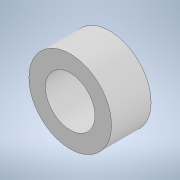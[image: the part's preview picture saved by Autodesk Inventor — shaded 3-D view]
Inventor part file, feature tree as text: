
AUTODESK INVENTOR PART (.ipt)
format: ipt  version: 2022 (Build 260153000, 153)  size: 98,816 bytes
history: native  units: mm
features: extrude x1, sketch x1
ambient origin geometry x8: Origin, YZ Plane, XZ Plane, XY Plane, X Axis, Y Axis, Z Axis, Center Point
bodies: Solid1 (feature_tree)
feature tree (2):
  extrude  "Extrusion1"  Depth=12.0mm
  sketch  "Sketch1"  dims[d0=15.0mm d1=25.0mm d2=12.0mm d3=0.0mm]
